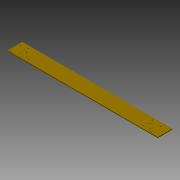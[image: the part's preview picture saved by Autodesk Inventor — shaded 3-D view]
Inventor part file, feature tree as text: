
AUTODESK INVENTOR PART (.ipt)
format: ipt  version: 2013 SP2 (Build 170200200, 200)  size: 108,544 bytes
history: native  units: mm
features: reference x10, extrude x2, sketch x2
ambient origin geometry x8: Origin, YZ Plane, XZ Plane, XY Plane, X Axis, Y Axis, Z Axis, Center Point
bodies: Solid1 (feature_tree)
feature tree (14):
  extrude  "Extrusion1"  Depth=3.0mm
  extrude  "Extrusion2"  Depth=10.0mm TaperAngle=0.0deg
  sketch  "Sketch1"  dims[d0=50.0mm d1=3.0mm]
  sketch  "Sketch2"  dims[d2=510.0mm d3=0.0mm d10=10.0mm d11=0.0mm d12=31.0mm d13=31.0mm d14=30.0mm d15=3.0mm d16=3.0mm d17=3.0mm d18=3.0mm d26=3.0mm d27=10.0mm d35=23.0mm]
  reference  "Reference23"
  reference  "Reference24"
  reference  "Reference25"
  reference  "Reference26"
  reference  "Reference27"
  reference  "Reference28"
  reference  "Reference31"
  reference  "Reference32"
  reference  "Reference33"
  reference  "Reference34"
